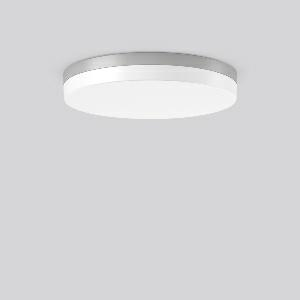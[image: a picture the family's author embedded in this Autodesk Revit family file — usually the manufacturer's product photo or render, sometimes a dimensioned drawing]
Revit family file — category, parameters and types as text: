
# Revit family: flat_slim_round_312634_004_19_adc9
name_source: partatom
category: Lighting Fixtures
units: mm (PartAtom-declared; Revit-internal decimal feet)

## family parameters
Cut with Voids When Loaded = No
Host = Face
Light Source = No
Part Type = Normal
Room Calculation Point = No
Round Connector Dimension = Use Diameter
Shared = No

## types (1)
- MultiLumen 1 830 (1 x LED Modul 830, 3450 lm, 3000)
    Apparent Load = 26 VA
    CIE Flux Codes = 40 71 90 84 100
    Color Rendering = 80
    Color Temperature = 3000
    Default Elevation = 1800 mm
    Height = 70 mm
    Lamp = 1 x LED Modul 830
    Lamp Light Flux = 3450 lm
    Lamp count = 1
    Length = 480 mm
    Lifetime = 50000 h
    Luminous efficacy = 133 lm/W
    Manufacturer = RZB
    ModVariant = No
    Model = 312634.004.19
    Mounting Place = Ceiling
    Mounting Type = Surface mounted
    Number of Poles = 1
    OnlyDefault = Yes
    Power Factor = 1
    Product Name = FLAT SLIM round
    Product group = Surface mounted ceiling and wall luminaires
    ProductGroupID = 305
    Protection Class = Protection class I
    Protection Degree = Degree of protection
    RLX_Detail_Level = 1
    RLX_Emergency_Light_Flux = 0 lm
    RLX_Emergency_Type = 0
    RLX_Emergency_Type_DB = No
    RlxData = <blob elided: 22613 chars, md5=939231f3>
    Socket = socket
    Standby Power = 0 W
    System Light Flux = 3450 lm
    System Power = 26 W
    Type Comments = MultiLumen 1 830
    Type Image = 312633.004.jpg
    URL = http://relux.com
    VarID = multilumen_1_830
    Voltage = 0 V
    Weight = 0.00 kg
    Width = 0 mm  [stored 0 ft]

note: [stored X ft] marks values corroborated as IEEE doubles in the binary element streams (Revit-internal decimal feet)

## geometry (parser evidence)
native form markers: Blend x4, Sweep x13
no freeform markers — native parametric forms only
